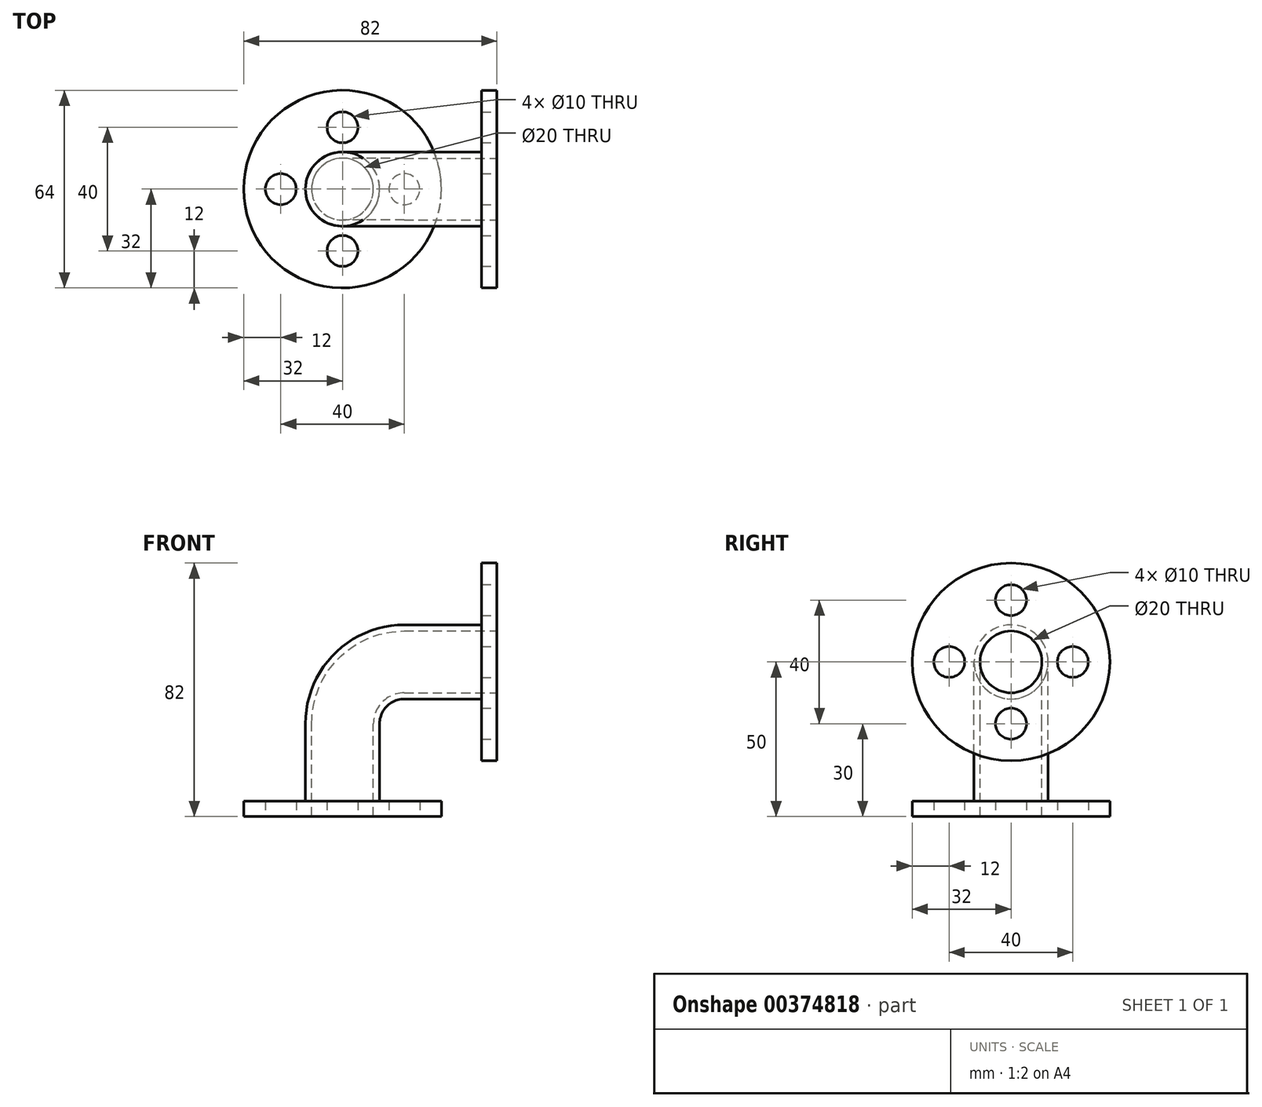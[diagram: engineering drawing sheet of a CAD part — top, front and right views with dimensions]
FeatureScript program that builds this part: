
annotation { "Feature Type Name" : "Feature", "Feature Type Description" : "" }
export const myFeature = defineFeature(function(context is Context, id is Id, definition is map)
    precondition{}
    {
        {
            var Q0;
            Q0=qCreatedBy(makeId("Front.planeOp"),FACE);
            var sketch = newSketch(context, id + "F0", { "sketchPlane" : qUnion([Q0])});
            skLineSegment(sketch, "E0", {"start": v(0, 0) * mm, "end": v(0, 30) * mm});
            skLineSegment(sketch, "E1", {"start": v(20, 50) * mm, "end": v(50, 50) * mm});
            skPoint(sketch, "E2.visualSharp", {"position": v(0, 50) * mm});
            skArc(sketch, "E2.filletArc", {"start": v(20, 50) * mm, "mid": v(5.86, 44.14) * mm, "end": v(0, 30) * mm});
            skSolve(sketch);
        }
        {
            var Q0;
            Q0=qCreatedBy(makeId("Top.planeOp"),FACE);
            var sketch = newSketch(context, id + "F1", { "sketchPlane" : qUnion([Q0])});
            skCircle(sketch, "E3", {"center": v(0, 0) * mm, "radius": 12 * mm});
            skSolve(sketch);
        }
        {
            var Q0;
            Q0=makeQuery(id+"F1.imprint","IMPRINT",FACE,{"disambiguationData":[TD([[makeQuery(id+"F1.imprint","IMPRINT",EDGE,{"derivedFrom":sQuery(id+"F1.wireOp",EDGE,"E3")}),1.0]])]});
            var Q1;
            Q1=sQuery(id+"F0.wireOp",EDGE,"E0");
            var Q2;
            Q2=sQuery(id+"F0.wireOp",EDGE,"E2.filletArc");
            var Q3;
            Q3=sQuery(id+"F0.wireOp",EDGE,"E1");
            sweep(context, id + "F2", {"profiles" : qUnion([Q0]), "path" : qUnion([Q1, Q2, Q3])});
        }
        {
            var Q0;
            Q0=makeQuery(id+"F2.opSweep","CAP_FACE",FACE,{"disambiguationData":[OSD([sQuery(id+"F0.wireOp",VERTEX,"E0.start"),sQuery(id+"F1.wireOp",EDGE,"E3")])],"isStart":true});
            var sketch = newSketch(context, id + "F3", { "sketchPlane" : qUnion([Q0])});
            skCircle(sketch, "E4", {"center": v(0, 0) * mm, "radius": 10 * mm});
            skSolve(sketch);
        }
        {
            var Q0;
            Q0=makeQuery(id+"F3.imprint","IMPRINT",FACE,{"disambiguationData":[TD([[makeQuery(id+"F3.imprint","IMPRINT",EDGE,{"derivedFrom":sQuery(id+"F3.wireOp",EDGE,"E4")}),1.0]])]});
            var Q1;
            Q1 = qConstructionFilter(qBodyType(qCreatedBy(id + "F0" ,EDGE), BodyType.WIRE), ConstructionObject.NO);
            sweep(context, id + "F4", {"operationType" : NewBodyOperationType.REMOVE, "profiles" : qUnion([Q0]), "path" : qUnion([Q1])});
        }
        {
            var Q0;
            Q0=makeQuery(id+"F2.opSweep","CAP_FACE",FACE,{"disambiguationData":[OSD([sQuery(id+"F0.wireOp",VERTEX,"E1.end"),sQuery(id+"F1.wireOp",EDGE,"E3")])],"isStart":false});
            var sketch = newSketch(context, id + "F5", { "sketchPlane" : qUnion([Q0])});
            skCircle(sketch, "E5", {"center": v(0, 50) * mm, "radius": 32 * mm});
            skSolve(sketch);
        }
        {
            var Q0;
            Q0=makeQuery(id+"F5.imprint","IMPRINT",FACE,{"disambiguationData":[TD([[makeQuery(id+"F5.imprint","IMPRINT",EDGE,{"derivedFrom":sQuery(id+"F5.wireOp",EDGE,"E5")}),1.0]])]});
            extrude(context, id + "F6", {"entities" : qUnion([Q0]), "operationType" : NewBodyOperationType.ADD, "oppositeDirection" : true, "depth" : 5 * mm});
        }
        {
            var Q0;
            Q0=makeQuery(id+"F2.opSweep","CAP_FACE",FACE,{"disambiguationData":[OSD([sQuery(id+"F0.wireOp",VERTEX,"E0.start"),sQuery(id+"F1.wireOp",EDGE,"E3")])],"isStart":true});
            var sketch = newSketch(context, id + "F7", { "sketchPlane" : qUnion([Q0])});
            skCircle(sketch, "E6", {"center": v(0, 0) * mm, "radius": 32 * mm});
            skSolve(sketch);
        }
        {
            var Q0;
            Q0=makeQuery(id+"F7.imprint","IMPRINT",FACE,{"disambiguationData":[TD([[makeQuery(id+"F7.imprint","IMPRINT",EDGE,{"derivedFrom":sQuery(id+"F7.wireOp",EDGE,"E6")}),1.0]])]});
            extrude(context, id + "F8", {"entities" : qUnion([Q0]), "operationType" : NewBodyOperationType.ADD, "oppositeDirection" : true, "depth" : 5 * mm});
        }
        {
            var Q0;
            {var subQ0=sQuery(id+"F1.wireOp",EDGE,"E3");var subQ1=sQuery(id+"F0.wireOp",VERTEX,"E1.end");Q0=makeQuery(id+"F6.boolean.opBoolean","MERGE",FACE,{"derivedFrom":[makeQuery(id+"F2.opSweep","CAP_FACE",FACE,{"disambiguationData":[OSD([subQ1,subQ0])],"isStart":false}),makeQuery(id+"F6.opExtrude","CAP_FACE",FACE,{"disambiguationData":[OSD([subQ1,subQ0,sQuery(id+"F5.wireOp",EDGE,"E5")])],"isStart":true})]});}
            var sketch = newSketch(context, id + "F9", { "sketchPlane" : qUnion([Q0])});
            skCircle(sketch, "E7", {"center": v(0, 70) * mm, "radius": 5 * mm});
            skLineSegment(sketch, "E8", {"start": v(0, 50) * mm, "end": v(0, 70) * mm, "construction": true});
            skLineSegment(sketch, "E9", {"start": v(0, 50) * mm, "end": v(0, 30) * mm, "construction": true});
            skLineSegment(sketch, "E10", {"start": v(0, 50) * mm, "end": v(20, 50) * mm, "construction": true});
            skLineSegment(sketch, "E11", {"start": v(0, 50) * mm, "end": v(-20, 50) * mm, "construction": true});
            skCircle(sketch, "E12", {"center": v(20, 50) * mm, "radius": 5 * mm});
            skCircle(sketch, "E13", {"center": v(0, 30) * mm, "radius": 5 * mm});
            skCircle(sketch, "E14", {"center": v(-20, 50) * mm, "radius": 5 * mm});
            skSolve(sketch);
        }
        {
            var Q0;
            Q0=makeQuery(id+"F9.imprint","IMPRINT",FACE,{"disambiguationData":[TD([[makeQuery(id+"F9.imprint","IMPRINT",EDGE,{"derivedFrom":sQuery(id+"F9.wireOp",EDGE,"E12")}),1.0]])]});
            var Q1;
            Q1=makeQuery(id+"F9.imprint","IMPRINT",FACE,{"disambiguationData":[TD([[makeQuery(id+"F9.imprint","IMPRINT",EDGE,{"derivedFrom":sQuery(id+"F9.wireOp",EDGE,"E7")}),1.0]])]});
            var Q2;
            Q2=makeQuery(id+"F9.imprint","IMPRINT",FACE,{"disambiguationData":[TD([[makeQuery(id+"F9.imprint","IMPRINT",EDGE,{"derivedFrom":sQuery(id+"F9.wireOp",EDGE,"E14")}),1.0]])]});
            var Q3;
            Q3=makeQuery(id+"F9.imprint","IMPRINT",FACE,{"disambiguationData":[TD([[makeQuery(id+"F9.imprint","IMPRINT",EDGE,{"derivedFrom":sQuery(id+"F9.wireOp",EDGE,"E13")}),1.0]])]});
            var Q4;
            Q4=makeQuery(id+"F6.opExtrude","CAP_FACE",FACE,{"disambiguationData":[OSD([sQuery(id+"F0.wireOp",VERTEX,"E1.end"),sQuery(id+"F1.wireOp",EDGE,"E3"),sQuery(id+"F5.wireOp",EDGE,"E5")])],"isStart":false});
            extrude(context, id + "F10", {"entities" : qUnion([Q0, Q1, Q2, Q3]), "operationType" : NewBodyOperationType.REMOVE, "endBound" : BoundingType.UP_TO_SURFACE, "oppositeDirection" : true, "endBoundEntityFace" : qUnion([Q4]), "depth" : 25 * mm});
        }
        {
            var Q0;
            {var subQ0=sQuery(id+"F1.wireOp",EDGE,"E3");var subQ1=sQuery(id+"F0.wireOp",VERTEX,"E0.start");Q0=makeQuery(id+"F8.boolean.opBoolean","MERGE",FACE,{"derivedFrom":[makeQuery(id+"F2.opSweep","CAP_FACE",FACE,{"disambiguationData":[OSD([subQ1,subQ0])],"isStart":true}),makeQuery(id+"F8.opExtrude","CAP_FACE",FACE,{"disambiguationData":[OSD([subQ1,subQ0,sQuery(id+"F7.wireOp",EDGE,"E6")])],"isStart":true})]});}
            var sketch = newSketch(context, id + "F11", { "sketchPlane" : qUnion([Q0])});
            skCircle(sketch, "E15", {"center": v(0, 20) * mm, "radius": 5 * mm});
            skCircle(sketch, "E16.1.0", {"center": v(-20, 0) * mm, "radius": 5 * mm});
            skCircle(sketch, "E16.2.0", {"center": v(0, -20) * mm, "radius": 5 * mm});
            skPoint(sketch, "E16.center", {"position": v(0, 0) * mm});
            skCircle(sketch, "E17.1.3.0", {"center": v(20, 0) * mm, "radius": 5 * mm});
            skSolve(sketch);
        }
        {
            var Q0;
            Q0=makeQuery(id+"F11.imprint","IMPRINT",FACE,{"disambiguationData":[TD([[makeQuery(id+"F11.imprint","IMPRINT",EDGE,{"derivedFrom":sQuery(id+"F11.wireOp",EDGE,"E17.1.3.0")}),1.0]])]});
            var Q1;
            Q1=makeQuery(id+"F11.imprint","IMPRINT",FACE,{"disambiguationData":[TD([[makeQuery(id+"F11.imprint","IMPRINT",EDGE,{"derivedFrom":sQuery(id+"F11.wireOp",EDGE,"E16.2.0")}),1.0]])]});
            var Q2;
            Q2=makeQuery(id+"F11.imprint","IMPRINT",FACE,{"disambiguationData":[TD([[makeQuery(id+"F11.imprint","IMPRINT",EDGE,{"derivedFrom":sQuery(id+"F11.wireOp",EDGE,"E16.1.0")}),1.0]])]});
            var Q3;
            Q3=makeQuery(id+"F11.imprint","IMPRINT",FACE,{"disambiguationData":[TD([[makeQuery(id+"F11.imprint","IMPRINT",EDGE,{"derivedFrom":sQuery(id+"F11.wireOp",EDGE,"E15")}),1.0]])]});
            var Q4;
            Q4=makeQuery(id+"F8.opExtrude","CAP_FACE",FACE,{"disambiguationData":[OSD([sQuery(id+"F0.wireOp",VERTEX,"E0.start"),sQuery(id+"F1.wireOp",EDGE,"E3"),sQuery(id+"F7.wireOp",EDGE,"E6")])],"isStart":false});
            extrude(context, id + "F12", {"entities" : qUnion([Q0, Q1, Q2, Q3]), "operationType" : NewBodyOperationType.REMOVE, "endBound" : BoundingType.UP_TO_SURFACE, "oppositeDirection" : true, "endBoundEntityFace" : qUnion([Q4]), "depth" : 25 * mm});
        }
    });
